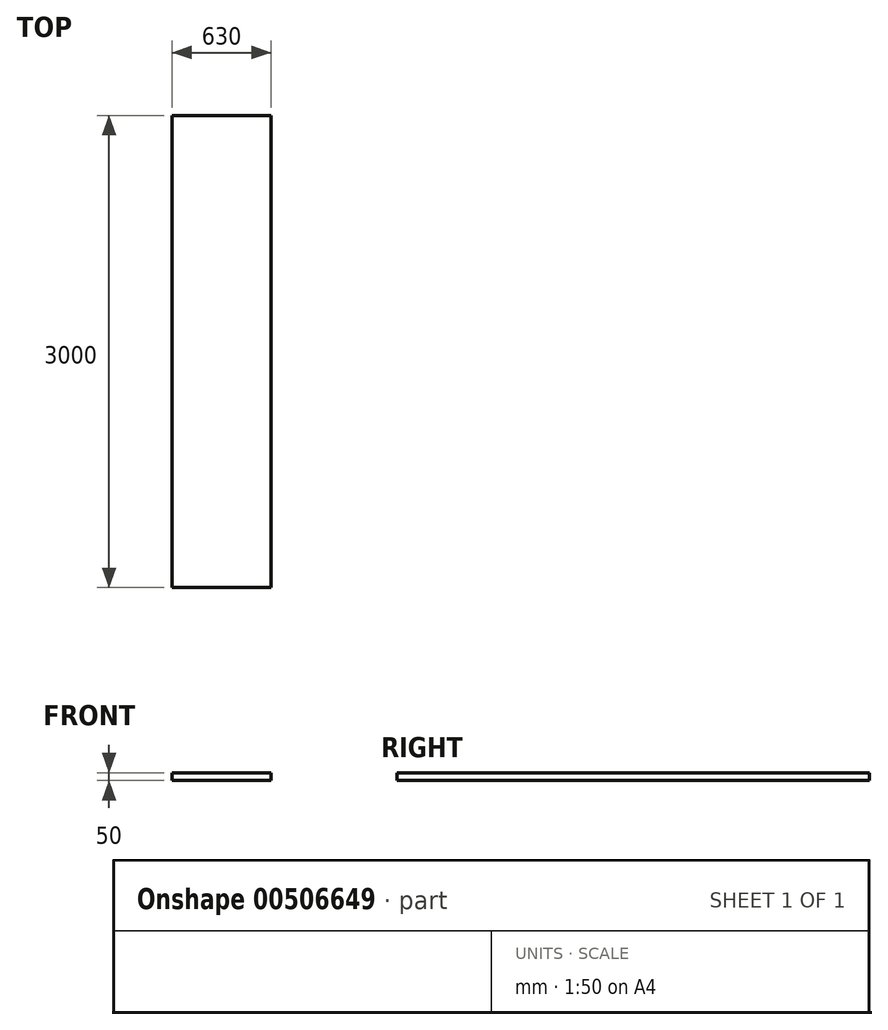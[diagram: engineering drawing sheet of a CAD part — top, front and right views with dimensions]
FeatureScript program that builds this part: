
annotation { "Feature Type Name" : "Feature", "Feature Type Description" : "" }
export const myFeature = defineFeature(function(context is Context, id is Id, definition is map)
    precondition{}
    {
        {
            var Q0;
            Q0=qCreatedBy(makeId("Right.planeOp"),FACE);
            var sketch = newSketch(context, id + "F0", { "sketchPlane" : qUnion([Q0])});
            skLineSegment(sketch, "E0.bottom", {"start": v(0, 0) * mm, "end": v(-3000, 0) * mm});
            skLineSegment(sketch, "E0.top", {"start": v(0, 50) * mm, "end": v(-3000, 50) * mm});
            skLineSegment(sketch, "E0.left", {"start": v(0, 0) * mm, "end": v(0, 50) * mm});
            skLineSegment(sketch, "E0.right", {"start": v(-3000, 0) * mm, "end": v(-3000, 50) * mm});
            skSolve(sketch);
        }
        {
            var Q0;
            Q0 = qSketchRegion(id + "F0", true);
            extrude(context, id + "F1", {"entities" : qUnion([Q0]), "depth" : 630 * mm});
        }
    });
